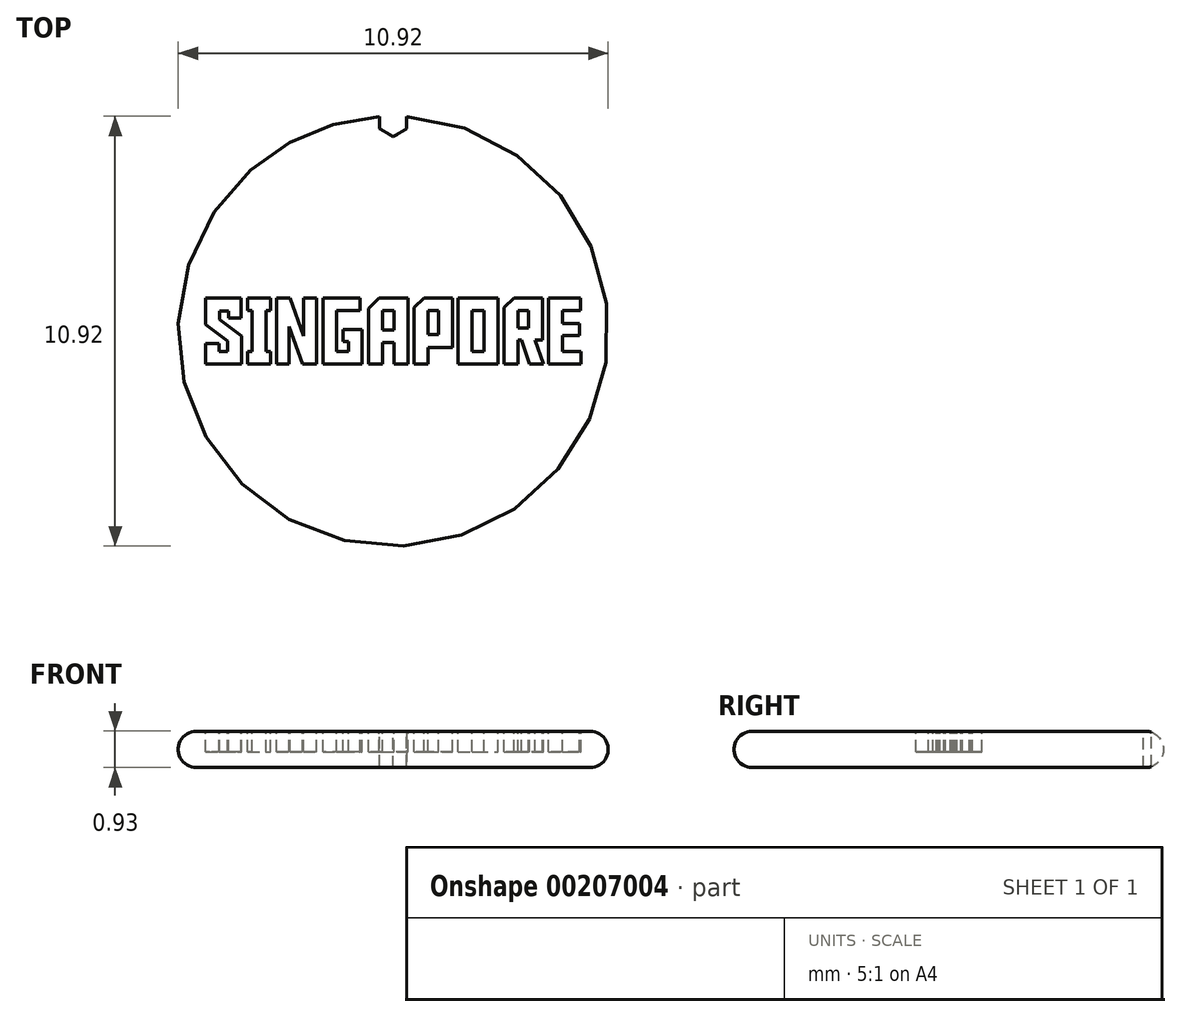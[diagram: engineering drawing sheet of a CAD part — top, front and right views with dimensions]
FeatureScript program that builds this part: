
annotation { "Feature Type Name" : "Feature", "Feature Type Description" : "" }
export const myFeature = defineFeature(function(context is Context, id is Id, definition is map)
    precondition{}
    {
        {
            var Q0;
            Q0=qCreatedBy(makeId("Front.planeOp"),FACE);
            var sketch = newSketch(context, id + "F0", { "sketchPlane" : qUnion([Q0])});
            skLineSegment(sketch, "E0.bottom", {"start": v(0, 0) * mm, "end": v(-5, 0) * mm});
            skLineSegment(sketch, "E0.top", {"start": v(0, 0.93) * mm, "end": v(-5, 0.93) * mm});
            skLineSegment(sketch, "E0.left", {"start": v(0, 0) * mm, "end": v(0, 0.93) * mm});
            skLineSegment(sketch, "E0.right", {"start": v(-5, 0) * mm, "end": v(-5, 0.93) * mm});
            skArc(sketch, "E1", {"start": v(-5, 0.93) * mm, "mid": v(-5.46, 0.46) * mm, "end": v(-5, 0) * mm});
            skSolve(sketch);
        }
        {
            var Q0;
            Q0 = qSketchRegion(id + "F0", true);
            var Q1;
            Q1=sQuery(id+"F0.wireOp",EDGE,"E0.left");
            revolve(context, id + "F1", {"entities" : qUnion([Q0]), "axis" : qUnion([Q1]), "revolveType" : RevolveType.FULL});
        }
        {
            var Q0;
            Q0=qCreatedBy(makeId("Top.planeOp"),FACE);
            cPlane(context, id + "F2", {"entities" : qUnion([Q0]), "cplaneType" : CPlaneType.OFFSET, "offset" : 1.2 * mm, "width" : 152.4 * mm, "height" : 152.4 * mm});
        }
        {
            var Q0;
            Q0=qCreatedBy(id+"F2.planeOp",FACE);
            var sketch = newSketch(context, id + "F3", { "sketchPlane" : qUnion([Q0])});
            skLineSegment(sketch, "E2", {"start": v(-3.85, -0.84) * mm, "end": v(-4.77, -0.84) * mm});
            skLineSegment(sketch, "E3", {"start": v(-4.77, -0.84) * mm, "end": v(-4.77, -0.32) * mm});
            skLineSegment(sketch, "E4", {"start": v(-4.77, -0.32) * mm, "end": v(-4.42, -0.32) * mm});
            skLineSegment(sketch, "E5", {"start": v(-4.42, -0.32) * mm, "end": v(-4.42, -0.52) * mm});
            skLineSegment(sketch, "E6", {"start": v(-4.42, -0.52) * mm, "end": v(-4.2, -0.52) * mm});
            skLineSegment(sketch, "E7", {"start": v(-4.2, -0.52) * mm, "end": v(-4.2, -0.25) * mm});
            skLineSegment(sketch, "E8", {"start": v(-4.2, -0.25) * mm, "end": v(-4.76, 0.17) * mm});
            skLineSegment(sketch, "E9", {"start": v(-4.76, 0.17) * mm, "end": v(-4.76, 0.84) * mm});
            skLineSegment(sketch, "E10", {"start": v(-4.76, 0.84) * mm, "end": v(-3.86, 0.84) * mm});
            skLineSegment(sketch, "E11", {"start": v(-3.86, 0.84) * mm, "end": v(-3.86, 0.34) * mm});
            skLineSegment(sketch, "E12", {"start": v(-3.86, 0.34) * mm, "end": v(-4.18, 0.34) * mm});
            skLineSegment(sketch, "E13", {"start": v(-4.18, 0.34) * mm, "end": v(-4.18, 0.52) * mm});
            skLineSegment(sketch, "E14", {"start": v(-4.18, 0.52) * mm, "end": v(-4.41, 0.52) * mm});
            skLineSegment(sketch, "E15", {"start": v(-4.41, 0.52) * mm, "end": v(-4.41, 0.3) * mm});
            skLineSegment(sketch, "E16", {"start": v(-4.41, 0.3) * mm, "end": v(-3.85, -0.12) * mm});
            skLineSegment(sketch, "E17", {"start": v(-3.85, -0.12) * mm, "end": v(-3.85, -0.84) * mm});
            skLineSegment(sketch, "E18", {"start": v(-3.12, -0.52) * mm, "end": v(-3.12, -0.84) * mm});
            skLineSegment(sketch, "E19", {"start": v(-3.12, -0.84) * mm, "end": v(-3.7, -0.84) * mm});
            skLineSegment(sketch, "E20", {"start": v(-3.7, -0.84) * mm, "end": v(-3.7, -0.52) * mm});
            skLineSegment(sketch, "E21", {"start": v(-3.7, -0.52) * mm, "end": v(-3.59, -0.52) * mm});
            skLineSegment(sketch, "E22", {"start": v(-3.59, -0.52) * mm, "end": v(-3.59, 0.52) * mm});
            skLineSegment(sketch, "E23", {"start": v(-3.59, 0.52) * mm, "end": v(-3.7, 0.52) * mm});
            skLineSegment(sketch, "E24", {"start": v(-3.7, 0.52) * mm, "end": v(-3.7, 0.84) * mm});
            skLineSegment(sketch, "E25", {"start": v(-3.7, 0.84) * mm, "end": v(-3.12, 0.84) * mm});
            skLineSegment(sketch, "E26", {"start": v(-3.12, 0.84) * mm, "end": v(-3.12, 0.52) * mm});
            skLineSegment(sketch, "E27", {"start": v(-3.12, 0.52) * mm, "end": v(-3.24, 0.52) * mm});
            skLineSegment(sketch, "E28", {"start": v(-3.24, 0.52) * mm, "end": v(-3.24, -0.52) * mm});
            skLineSegment(sketch, "E29", {"start": v(-3.24, -0.52) * mm, "end": v(-3.12, -0.52) * mm});
            skLineSegment(sketch, "E30", {"start": v(-2.28, -0.12) * mm, "end": v(-2.28, 0.84) * mm});
            skLineSegment(sketch, "E31", {"start": v(-2.28, 0.84) * mm, "end": v(-1.95, 0.84) * mm});
            skLineSegment(sketch, "E32", {"start": v(-1.95, 0.84) * mm, "end": v(-1.95, -0.84) * mm});
            skLineSegment(sketch, "E33", {"start": v(-1.95, -0.84) * mm, "end": v(-2.3, -0.84) * mm});
            skLineSegment(sketch, "E34", {"start": v(-2.3, -0.84) * mm, "end": v(-2.64, 0.12) * mm});
            skLineSegment(sketch, "E35", {"start": v(-2.64, 0.12) * mm, "end": v(-2.64, -0.84) * mm});
            skLineSegment(sketch, "E36", {"start": v(-2.64, -0.84) * mm, "end": v(-2.97, -0.84) * mm});
            skLineSegment(sketch, "E37", {"start": v(-2.97, -0.84) * mm, "end": v(-2.97, 0.84) * mm});
            skLineSegment(sketch, "E38", {"start": v(-2.97, 0.84) * mm, "end": v(-2.62, 0.84) * mm});
            skLineSegment(sketch, "E39", {"start": v(-2.62, 0.84) * mm, "end": v(-2.28, -0.12) * mm});
            skLineSegment(sketch, "E40", {"start": v(-1.13, -0.52) * mm, "end": v(-1.13, -0.26) * mm});
            skLineSegment(sketch, "E41", {"start": v(-1.13, -0.26) * mm, "end": v(-1.28, -0.26) * mm});
            skLineSegment(sketch, "E42", {"start": v(-1.28, -0.26) * mm, "end": v(-1.28, 0.04) * mm});
            skLineSegment(sketch, "E43", {"start": v(-1.28, 0.04) * mm, "end": v(-0.79, 0.04) * mm});
            skLineSegment(sketch, "E44", {"start": v(-0.79, 0.04) * mm, "end": v(-0.79, -0.84) * mm});
            skLineSegment(sketch, "E45", {"start": v(-0.79, -0.84) * mm, "end": v(-1.79, -0.84) * mm});
            skLineSegment(sketch, "E46", {"start": v(-1.79, -0.84) * mm, "end": v(-1.79, 0.84) * mm});
            skLineSegment(sketch, "E47", {"start": v(-1.79, 0.84) * mm, "end": v(-0.84, 0.84) * mm});
            skLineSegment(sketch, "E48", {"start": v(-0.84, 0.84) * mm, "end": v(-0.84, 0.52) * mm});
            skLineSegment(sketch, "E49", {"start": v(-0.84, 0.52) * mm, "end": v(-1.43, 0.52) * mm});
            skLineSegment(sketch, "E50", {"start": v(-1.43, 0.52) * mm, "end": v(-1.43, -0.52) * mm});
            skLineSegment(sketch, "E51", {"start": v(-1.43, -0.52) * mm, "end": v(-1.13, -0.52) * mm});
            skLineSegment(sketch, "E52", {"start": v(-0.27, -0.84) * mm, "end": v(-0.63, -0.84) * mm});
            skLineSegment(sketch, "E53", {"start": v(-0.63, -0.84) * mm, "end": v(-0.63, 0.57) * mm});
            skLineSegment(sketch, "E54", {"start": v(-0.63, 0.57) * mm, "end": v(-0.36, 0.84) * mm});
            skLineSegment(sketch, "E55", {"start": v(-0.36, 0.84) * mm, "end": v(0.38, 0.84) * mm});
            skLineSegment(sketch, "E56", {"start": v(0.38, 0.84) * mm, "end": v(0.38, -0.84) * mm});
            skLineSegment(sketch, "E57", {"start": v(0.38, -0.84) * mm, "end": v(0.02, -0.84) * mm});
            skLineSegment(sketch, "E58", {"start": v(0.02, -0.84) * mm, "end": v(0.02, -0.29) * mm});
            skLineSegment(sketch, "E59", {"start": v(0.02, -0.29) * mm, "end": v(-0.27, -0.29) * mm});
            skLineSegment(sketch, "E60", {"start": v(-0.27, -0.29) * mm, "end": v(-0.27, -0.84) * mm});
            skLineSegment(sketch, "E61", {"start": v(0.02, 0.03) * mm, "end": v(0.02, 0.52) * mm});
            skLineSegment(sketch, "E62", {"start": v(0.02, 0.52) * mm, "end": v(-0.27, 0.52) * mm});
            skLineSegment(sketch, "E63", {"start": v(-0.27, 0.52) * mm, "end": v(-0.27, 0.03) * mm});
            skLineSegment(sketch, "E64", {"start": v(-0.27, 0.03) * mm, "end": v(0.02, 0.03) * mm});
            skLineSegment(sketch, "E65", {"start": v(0.88, -0.84) * mm, "end": v(0.53, -0.84) * mm});
            skLineSegment(sketch, "E66", {"start": v(0.53, -0.84) * mm, "end": v(0.53, 0.6) * mm});
            skLineSegment(sketch, "E67", {"start": v(0.53, 0.6) * mm, "end": v(0.79, 0.84) * mm});
            skLineSegment(sketch, "E68", {"start": v(0.79, 0.84) * mm, "end": v(1.5, 0.84) * mm});
            skLineSegment(sketch, "E69", {"start": v(1.5, 0.84) * mm, "end": v(1.5, -0.41) * mm});
            skLineSegment(sketch, "E70", {"start": v(1.5, -0.41) * mm, "end": v(0.88, -0.41) * mm});
            skLineSegment(sketch, "E71", {"start": v(0.88, -0.41) * mm, "end": v(0.88, -0.84) * mm});
            skLineSegment(sketch, "E72", {"start": v(1.15, -0.1) * mm, "end": v(1.15, 0.52) * mm});
            skLineSegment(sketch, "E73", {"start": v(1.15, 0.52) * mm, "end": v(0.88, 0.52) * mm});
            skLineSegment(sketch, "E74", {"start": v(0.88, 0.52) * mm, "end": v(0.88, -0.1) * mm});
            skLineSegment(sketch, "E75", {"start": v(0.88, -0.1) * mm, "end": v(1.15, -0.1) * mm});
            skLineSegment(sketch, "E76", {"start": v(1.65, 0.84) * mm, "end": v(2.66, 0.84) * mm});
            skLineSegment(sketch, "E77", {"start": v(2.66, 0.84) * mm, "end": v(2.66, -0.84) * mm});
            skLineSegment(sketch, "E78", {"start": v(2.66, -0.84) * mm, "end": v(1.65, -0.84) * mm});
            skLineSegment(sketch, "E79", {"start": v(1.65, -0.84) * mm, "end": v(1.65, 0.84) * mm});
            skLineSegment(sketch, "E80", {"start": v(2, -0.52) * mm, "end": v(2.31, -0.52) * mm});
            skLineSegment(sketch, "E81", {"start": v(2.31, -0.52) * mm, "end": v(2.31, 0.52) * mm});
            skLineSegment(sketch, "E82", {"start": v(2.31, 0.52) * mm, "end": v(2, 0.52) * mm});
            skLineSegment(sketch, "E83", {"start": v(2, 0.52) * mm, "end": v(2, -0.52) * mm});
            skLineSegment(sketch, "E84", {"start": v(3.47, -0.84) * mm, "end": v(3.26, -0.23) * mm});
            skLineSegment(sketch, "E85", {"start": v(3.26, -0.23) * mm, "end": v(3.17, -0.23) * mm});
            skLineSegment(sketch, "E86", {"start": v(3.17, -0.23) * mm, "end": v(3.17, -0.84) * mm});
            skLineSegment(sketch, "E87", {"start": v(3.17, -0.84) * mm, "end": v(2.82, -0.84) * mm});
            skLineSegment(sketch, "E88", {"start": v(2.82, -0.84) * mm, "end": v(2.82, 0.6) * mm});
            skLineSegment(sketch, "E89", {"start": v(2.82, 0.6) * mm, "end": v(3.07, 0.84) * mm});
            skLineSegment(sketch, "E90", {"start": v(3.07, 0.84) * mm, "end": v(3.79, 0.84) * mm});
            skLineSegment(sketch, "E91", {"start": v(3.79, 0.84) * mm, "end": v(3.79, -0.23) * mm});
            skLineSegment(sketch, "E92", {"start": v(3.79, -0.23) * mm, "end": v(3.6, -0.23) * mm});
            skLineSegment(sketch, "E93", {"start": v(3.6, -0.23) * mm, "end": v(3.82, -0.84) * mm});
            skLineSegment(sketch, "E94", {"start": v(3.82, -0.84) * mm, "end": v(3.47, -0.84) * mm});
            skLineSegment(sketch, "E95", {"start": v(3.44, 0.08) * mm, "end": v(3.44, 0.52) * mm});
            skLineSegment(sketch, "E96", {"start": v(3.44, 0.52) * mm, "end": v(3.17, 0.52) * mm});
            skLineSegment(sketch, "E97", {"start": v(3.17, 0.52) * mm, "end": v(3.17, 0.08) * mm});
            skLineSegment(sketch, "E98", {"start": v(3.17, 0.08) * mm, "end": v(3.44, 0.08) * mm});
            skLineSegment(sketch, "E99", {"start": v(3.95, 0.84) * mm, "end": v(4.76, 0.84) * mm});
            skLineSegment(sketch, "E100", {"start": v(3.8, 0.84) * mm, "end": v(3.8, 0.52) * mm});
            skLineSegment(sketch, "E101", {"start": v(4.76, 0.52) * mm, "end": v(4.3, 0.52) * mm});
            skLineSegment(sketch, "E102", {"start": v(4.3, 0.52) * mm, "end": v(4.3, 0.2) * mm});
            skLineSegment(sketch, "E103", {"start": v(4.3, 0.2) * mm, "end": v(4.74, 0.2) * mm});
            skLineSegment(sketch, "E104", {"start": v(4.74, 0.2) * mm, "end": v(4.74, -0.12) * mm});
            skLineSegment(sketch, "E105", {"start": v(4.74, -0.12) * mm, "end": v(4.3, -0.12) * mm});
            skLineSegment(sketch, "E106", {"start": v(4.3, -0.12) * mm, "end": v(4.3, -0.52) * mm});
            skLineSegment(sketch, "E107", {"start": v(4.3, -0.52) * mm, "end": v(4.77, -0.52) * mm});
            skLineSegment(sketch, "E108", {"start": v(4.77, -0.84) * mm, "end": v(3.95, -0.84) * mm});
            skLineSegment(sketch, "E109", {"start": v(3.95, -0.84) * mm, "end": v(3.95, 0.84) * mm});
            skLineSegment(sketch, "E110", {"start": v(4.76, 0.84) * mm, "end": v(4.76, 0.52) * mm});
            skLineSegment(sketch, "E111", {"start": v(4.77, -0.52) * mm, "end": v(4.77, -0.84) * mm});
            skSolve(sketch);
        }
        {
            var Q0;
            Q0 = qSketchRegion(id + "F3", true);
            extrude(context, id + "F4", {"entities" : qUnion([Q0]), "operationType" : NewBodyOperationType.REMOVE, "oppositeDirection" : true, "depth" : 0.8 * mm});
        }
        {
            var Q0;
            Q0=qCreatedBy(id+"F2.planeOp",FACE);
            var sketch = newSketch(context, id + "F5", { "sketchPlane" : qUnion([Q0])});
            skCircle(sketch, "E112.cCircle", {"center": v(0, 5.34) * mm, "radius": 0.34 * mm, "construction": true});
            skLineSegment(sketch, "E112.0", {"start": v(0.34, 5.54) * mm, "end": v(0.34, 5.14) * mm});
            skLineSegment(sketch, "E112.1", {"start": v(0.34, 5.14) * mm, "end": v(0, 4.94) * mm});
            skLineSegment(sketch, "E112.2", {"start": v(0, 4.94) * mm, "end": v(-0.34, 5.14) * mm});
            skLineSegment(sketch, "E112.3", {"start": v(-0.34, 5.14) * mm, "end": v(-0.34, 5.54) * mm});
            skLineSegment(sketch, "E112.4", {"start": v(-0.34, 5.54) * mm, "end": v(0, 5.74) * mm});
            skLineSegment(sketch, "E112.5", {"start": v(0, 5.74) * mm, "end": v(0.34, 5.54) * mm});
            skPoint(sketch, "E112.0.midPoint", {"position": v(0.34, 5.34) * mm});
            skSolve(sketch);
        }
        {
            var Q0;
            Q0 = qSketchRegion(id + "F5", true);
            extrude(context, id + "F6", {"entities" : qUnion([Q0]), "operationType" : NewBodyOperationType.REMOVE, "oppositeDirection" : true, "depth" : 25.4 * mm});
        }
    });
